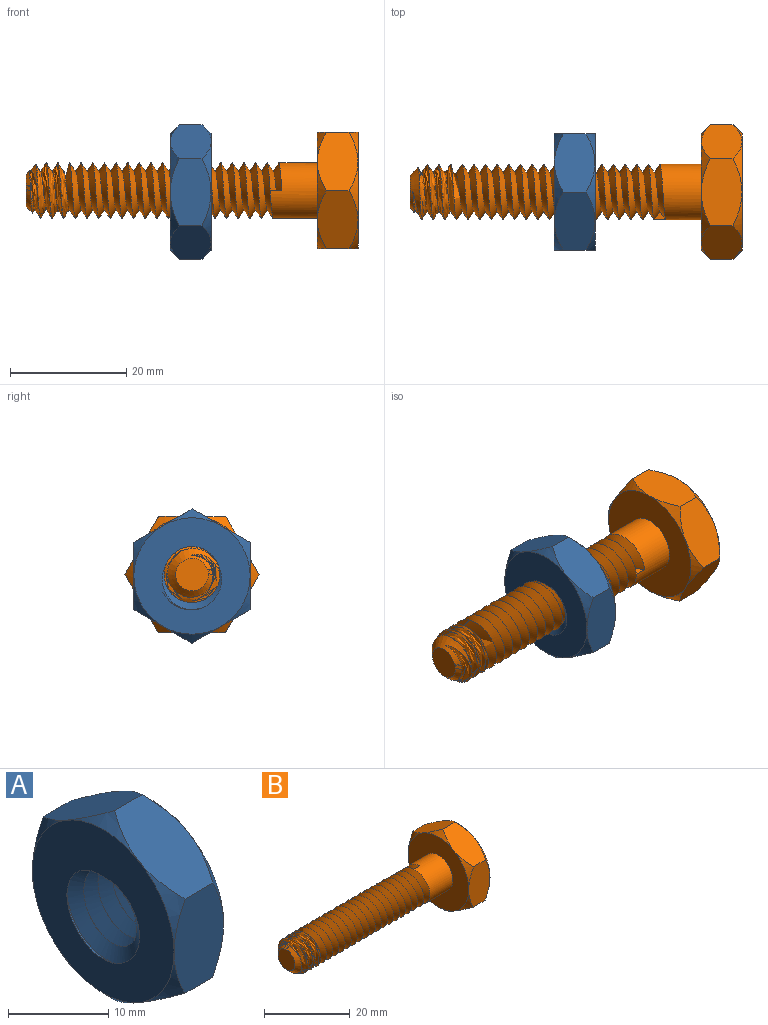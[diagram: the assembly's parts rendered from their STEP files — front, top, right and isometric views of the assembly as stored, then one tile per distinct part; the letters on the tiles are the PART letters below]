
ASSEMBLY  parts=2 mates=1
PART A: 13 faces, bbox 10.6x24.2x24.2 mm
  f0: plane 21.13x21.13mm, normal (1,0,0), area 232.3mm2, adj f1,f10,f11,f12
  f1: cone r=13.5mm half-angle=45deg, axis (-1,0,0), area 45.6mm2, adj f0,f2,f3,f4,f5,f6,f7
  f2: plane 10.02x7.01mm, normal (0,0.5,0.87), area 68.6mm2, adj f1,f3,f7,f8
  f3: plane 9.98x7.01mm, normal (0,-0.5,0.86), area 68.6mm2, adj f1,f2,f4,f8
  f4: plane 11.55x7.01mm, normal (0,-1,0), area 68.6mm2, adj f1,f3,f5,f8
  f5: plane 10.02x7.01mm, normal (0,-0.5,-0.87), area 68.6mm2, adj f1,f4,f6,f8
  f6: plane 9.98x7.01mm, normal (0,0.5,-0.86), area 68.6mm2, adj f1,f5,f7,f8
  f7: plane 11.55x7.01mm, normal (0,1,0), area 68.6mm2, adj f1,f2,f6,f8
  f8: cone r=7.94mm half-angle=45deg, axis (1,0,0), area 45.6mm2, adj f2,f3,f4,f5,f6,f7,f9
  f9: plane 21.13x21.13mm, normal (-1,0,0), area 232.3mm2, adj f8,f10,f11,f12
  f10: bspline ~13.53x11.72mm, area 33.5mm2, adj f0,f9,f11,f12
  f11: bspline ~13.32x11.53mm, area 196.2mm2, adj f0,f9,f10,f12
  f12: bspline ~13.32x11.53mm, area 196.2mm2, adj f0,f9,f10,f11
PART B: 26 faces, bbox 58.9x24.2x24.2 mm
  f0: cylinder r=4.8mm len=9.6mm, axis (1,0,0), area 214.1mm2, adj f1,f3,f7
  f1: plane 2x1.52mm, normal (0,1,0), area 1.5mm2, adj f0,f2,f3
  f2: bspline ~43.67x11.09mm, area 951.1mm2, adj f1,f3,f5
  f3: bspline ~44x11.09mm, area 970.9mm2, adj f0,f1,f2,f5
  f4: plane 5.6x5.6mm, normal (-1,0,0), area 24.6mm2, adj f5
  f5: cone r=4.8mm half-angle=45deg, axis (1,0,0), area 38.6mm2, adj f2,f3,f4
  f6: plane 20x20mm, normal (1,0,0), area 314.2mm2, adj f8,f9,f10,f11,f12,f13,f20,f21
  f7: plane 20x20mm, normal (-1,0,0), area 241.8mm2, adj f0,f8,f9,f10,f11,f12,f13,f14
  f8: plane 11.14x8.12mm, normal (0,0.5,0.87), area 68.6mm2, adj f6,f7,f9,f13,f16,f17,f22,f23
  f9: plane 11.1x8.12mm, normal (0,-0.5,0.86), area 68.6mm2, adj f6,f7,f8,f10,f17,f18,f23,f24
  f10: plane 12.66x8.11mm, normal (0,-1,0), area 68.6mm2, adj f6,f7,f9,f11,f18,f19,f24,f25
  f11: plane 11.14x8.12mm, normal (0,-0.5,-0.87), area 68.6mm2, adj f6,f7,f10,f12,f14,f19,f20,f25
  f12: plane 11.1x8.12mm, normal (0,0.5,-0.86), area 68.6mm2, adj f6,f7,f11,f13,f14,f15,f20,f21
  f13: plane 12.66x8.11mm, normal (0,1,0), area 68.6mm2, adj f6,f7,f8,f12,f15,f16,f21,f22
  f14: cone r=9.15mm half-angle=45deg, axis (1,0,0), area 12mm2, adj f7,f11,f12
  f15: cone r=9.15mm half-angle=45deg, axis (1,0,0), area 12mm2, adj f7,f12,f13
  f16: cone r=9.15mm half-angle=45deg, axis (1,0,0), area 12mm2, adj f7,f8,f13
  f17: cone r=9.15mm half-angle=45deg, axis (1,0,0), area 12mm2, adj f7,f8,f9
  f18: cone r=9.15mm half-angle=45deg, axis (1,0,0), area 12mm2, adj f7,f9,f10
  f19: cone r=9.15mm half-angle=45deg, axis (1,0,0), area 12mm2, adj f7,f10,f11
  f20: cone r=13.5mm half-angle=45deg, axis (-1,0,0), area 12mm2, adj f6,f11,f12
  f21: cone r=13.5mm half-angle=45deg, axis (-1,0,0), area 12mm2, adj f6,f12,f13
  f22: cone r=13.5mm half-angle=45deg, axis (-1,0,0), area 12mm2, adj f6,f8,f13
  f23: cone r=13.5mm half-angle=45deg, axis (-1,0,0), area 12mm2, adj f6,f8,f9
  f24: cone r=13.5mm half-angle=45deg, axis (-1,0,0), area 12mm2, adj f6,f9,f10
  f25: cone r=13.5mm half-angle=45deg, axis (-1,0,0), area 12mm2, adj f6,f10,f11
PLACE A t=(-60.59,-1.85,11.28)mm
PLACE B rot(axis=(1,0,0),90deg) t=(-42.31,-1.85,11.52)mm
MATE cylindrical B.f0 <-> A.f9  axis (-1,0,0) through (-92.41,-1.85,11.52)mm
